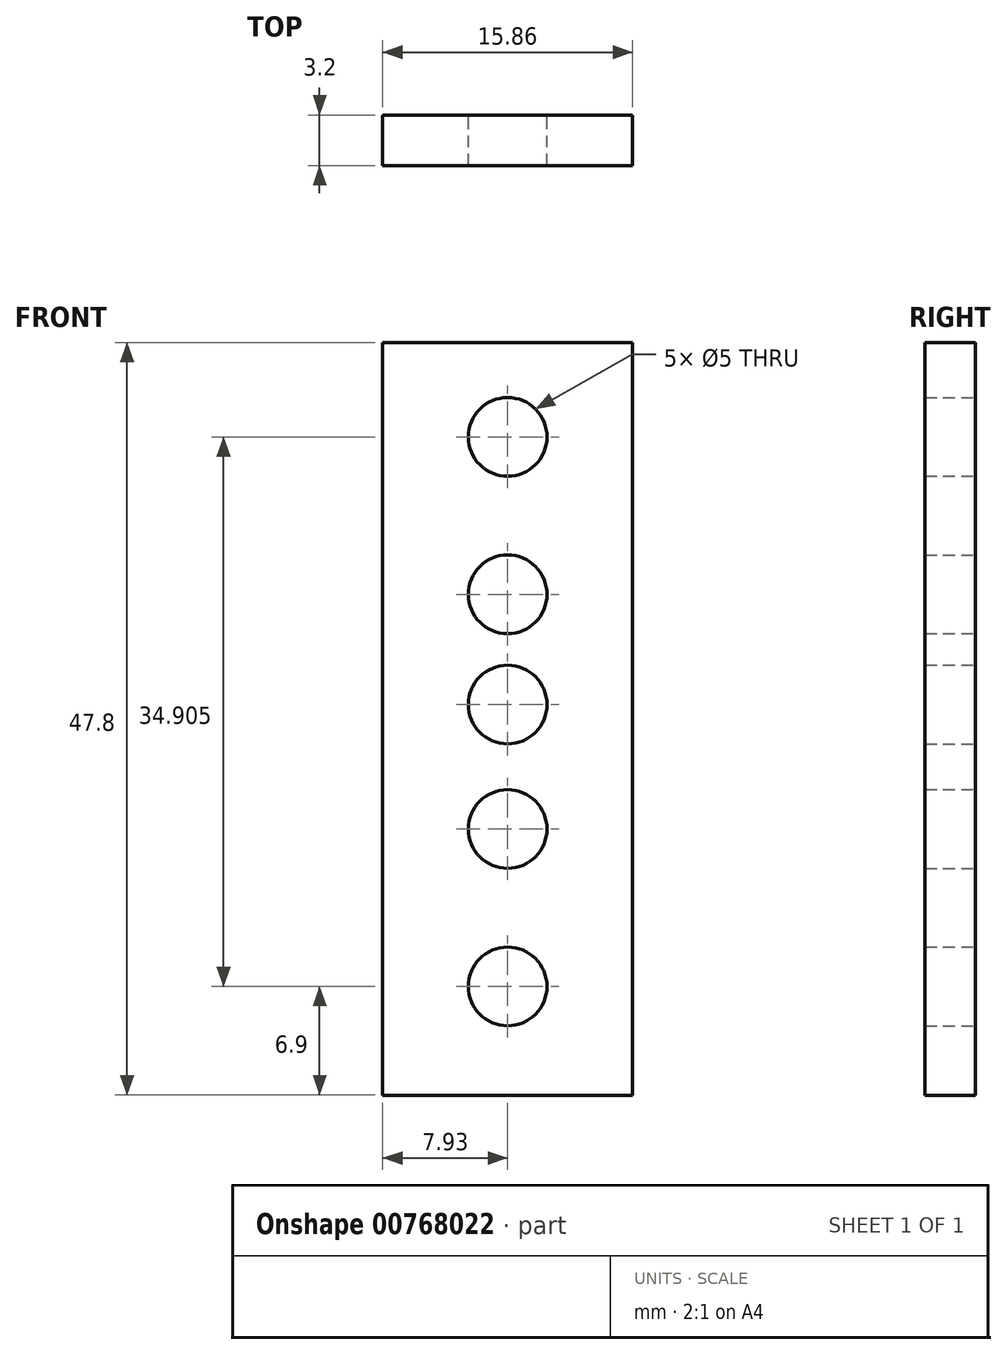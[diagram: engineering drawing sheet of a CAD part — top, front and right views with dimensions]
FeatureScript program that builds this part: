
annotation { "Feature Type Name" : "Feature", "Feature Type Description" : "" }
export const myFeature = defineFeature(function(context is Context, id is Id, definition is map)
    precondition{}
    {
        {
            var Q0;
            Q0=qCreatedBy(makeId("Front.planeOp"),FACE);
            var sketch = newSketch(context, id + "F0", { "sketchPlane" : qUnion([Q0])});
            skLineSegment(sketch, "E0.bottom", {"start": v(7.94, 23.9) * mm, "end": v(-7.93, 23.9) * mm});
            skLineSegment(sketch, "E0.top", {"start": v(7.93, -23.9) * mm, "end": v(-7.93, -23.9) * mm});
            skLineSegment(sketch, "E0.left", {"start": v(7.94, 23.9) * mm, "end": v(7.93, -23.9) * mm});
            skLineSegment(sketch, "E0.right", {"start": v(-7.93, 23.9) * mm, "end": v(-7.93, -23.9) * mm});
            skPoint(sketch, "E0.middle", {"position": v(0, 0) * mm});
            skCircle(sketch, "E1", {"center": v(0, 17.9) * mm, "radius": 2.5 * mm});
            skCircle(sketch, "E2", {"center": v(0, 7.9) * mm, "radius": 2.5 * mm});
            skCircle(sketch, "E3", {"center": v(0, 0.9) * mm, "radius": 2.5 * mm});
            skCircle(sketch, "E4", {"center": v(0, -7) * mm, "radius": 2.5 * mm});
            skCircle(sketch, "E5", {"center": v(0, -17) * mm, "radius": 2.5 * mm});
            skSolve(sketch);
        }
        {
            var Q0;
            Q0=makeQuery(id+"F0.imprint","IMPRINT",FACE,{"disambiguationData":[TD([[makeQuery(id+"F0.imprint","IMPRINT",EDGE,{"derivedFrom":sQuery(id+"F0.wireOp",EDGE,"E0.bottom")}),1.0]])]});
            extrude(context, id + "F1", {"entities" : qUnion([Q0]), "depth" : 3.2 * mm, "offsetDistance" : 25 * mm});
        }
    });
